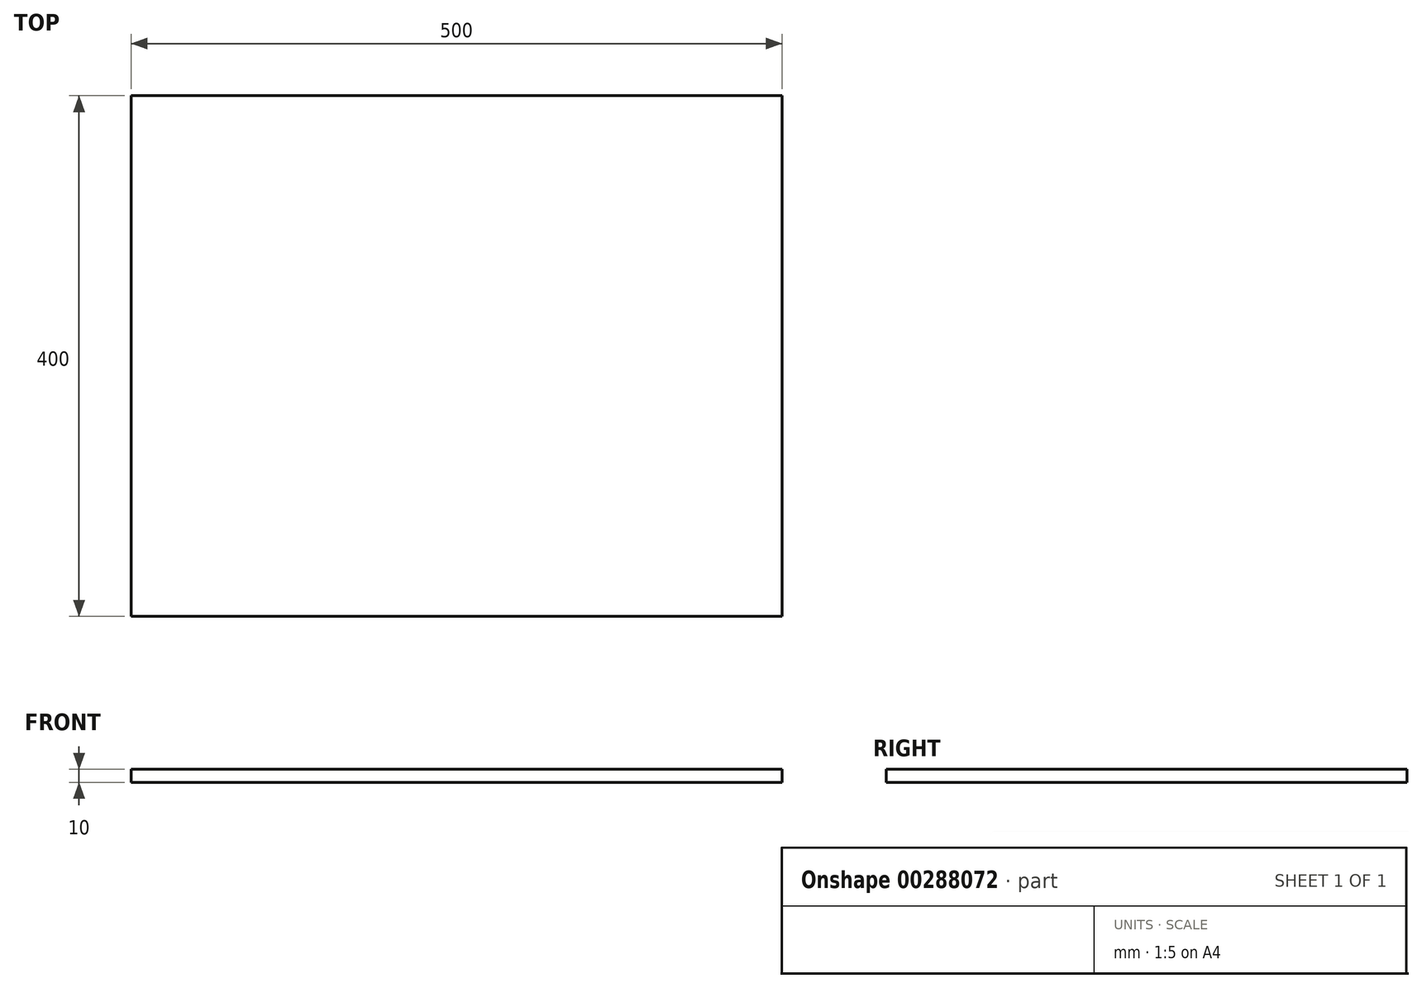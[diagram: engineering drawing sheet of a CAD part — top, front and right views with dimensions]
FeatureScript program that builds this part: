
annotation { "Feature Type Name" : "Feature", "Feature Type Description" : "" }
export const myFeature = defineFeature(function(context is Context, id is Id, definition is map)
    precondition{}
    {
        {
            var Q0;
            Q0=qCreatedBy(makeId("Top.planeOp"),FACE);
            var sketch = newSketch(context, id + "F0", { "sketchPlane" : qUnion([Q0])});
            skLineSegment(sketch, "E0.bottom", {"start": v(250, -200) * mm, "end": v(-250, -200) * mm});
            skLineSegment(sketch, "E0.top", {"start": v(250, 200) * mm, "end": v(-250, 200) * mm});
            skLineSegment(sketch, "E0.left", {"start": v(250, -200) * mm, "end": v(250, 200) * mm});
            skLineSegment(sketch, "E0.right", {"start": v(-250, -200) * mm, "end": v(-250, 200) * mm});
            skPoint(sketch, "E0.middle", {"position": v(0, 0) * mm});
            skSolve(sketch);
        }
        {
            var Q0;
            Q0 = qSketchRegion(id + "F0", true);
            extrude(context, id + "F1", {"entities" : qUnion([Q0]), "depth" : 10 * mm});
        }
    });
